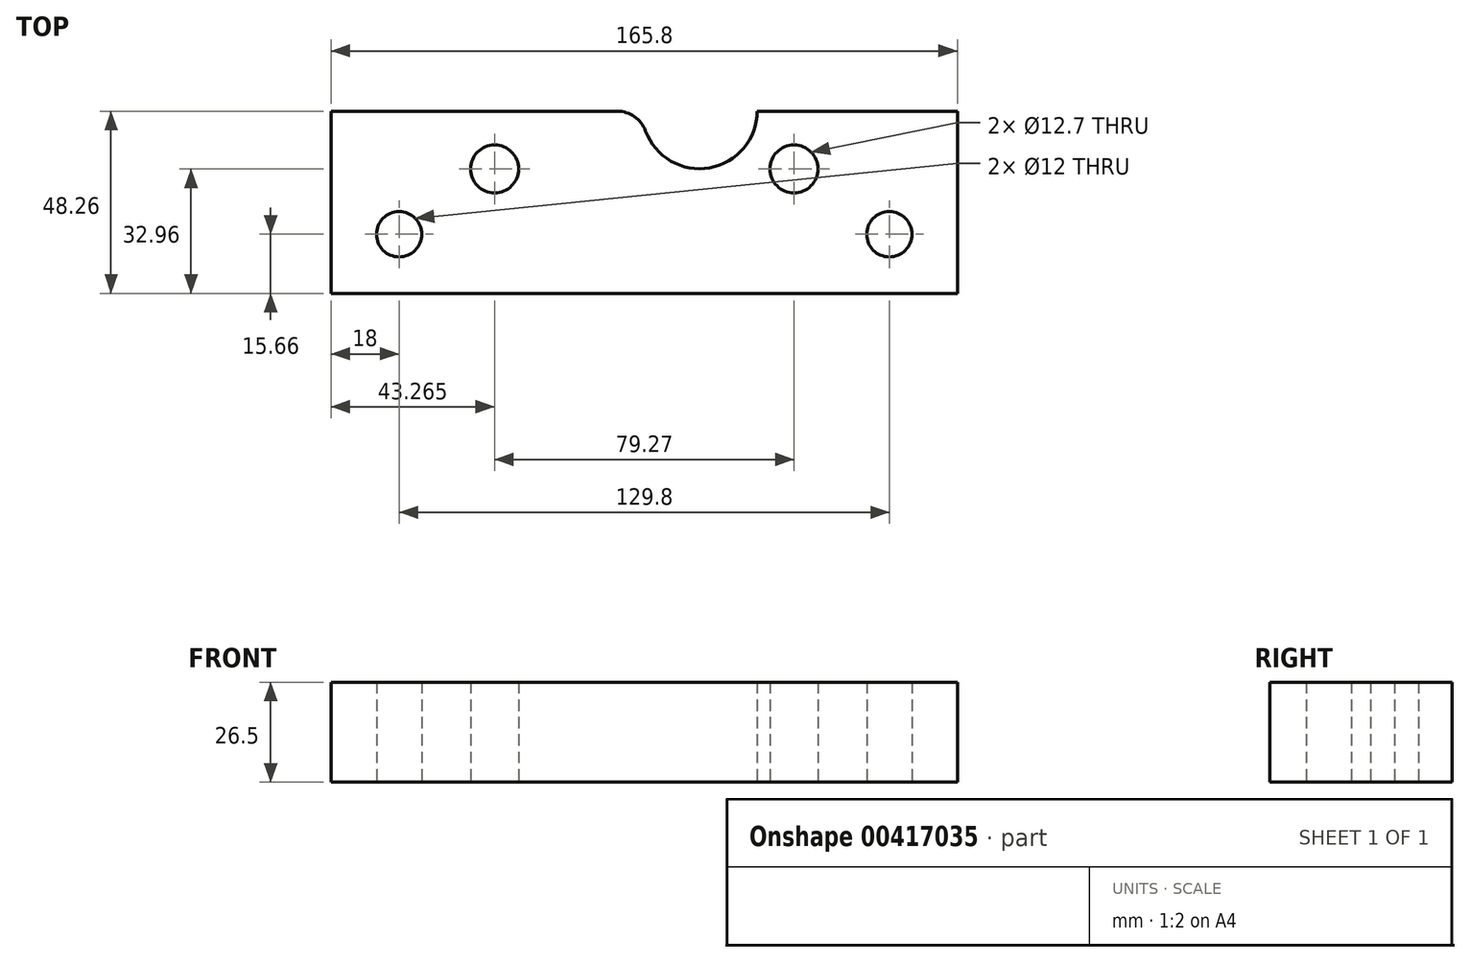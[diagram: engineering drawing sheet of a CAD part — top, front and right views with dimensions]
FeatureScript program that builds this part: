
annotation { "Feature Type Name" : "Feature", "Feature Type Description" : "" }
export const myFeature = defineFeature(function(context is Context, id is Id, definition is map)
    precondition{}
    {
        {
            var Q0;
            Q0=qCreatedBy(makeId("Top.planeOp"),FACE);
            var sketch = newSketch(context, id + "F0", { "sketchPlane" : qUnion([Q0])});
            skLineSegment(sketch, "E0.bottom", {"start": v(-82.9, 32.6) * mm, "end": v(-7.18, 32.6) * mm});
            skLineSegment(sketch, "E0.top", {"start": v(-82.9, -15.66) * mm, "end": v(82.9, -15.66) * mm});
            skLineSegment(sketch, "E0.left", {"start": v(-82.9, 32.6) * mm, "end": v(-82.9, -15.66) * mm});
            skLineSegment(sketch, "E0.right", {"start": v(82.9, 32.6) * mm, "end": v(82.9, -15.66) * mm});
            skCircle(sketch, "E1", {"center": v(-39.63, 17.3) * mm, "radius": 6.35 * mm});
            skCircle(sketch, "E2", {"center": v(39.63, 17.3) * mm, "radius": 6.35 * mm});
            skCircle(sketch, "E3", {"center": v(64.9, 0) * mm, "radius": 6 * mm});
            skCircle(sketch, "E4", {"center": v(-64.9, 0) * mm, "radius": 6 * mm});
            skPoint(sketch, "E5", {"position": v(-70.9, 0) * mm});
            skPoint(sketch, "E6", {"position": v(70.9, 0) * mm});
            skPoint(sketch, "E7", {"position": v(-58.9, 0) * mm});
            skPoint(sketch, "E8", {"position": v(58.9, 0) * mm});
            skPoint(sketch, "E9", {"position": v(-45.98, 17.3) * mm});
            skPoint(sketch, "E10", {"position": v(45.98, 17.3) * mm});
            skPoint(sketch, "E11", {"position": v(-33.28, 17.3) * mm});
            skPoint(sketch, "E12", {"position": v(33.28, 17.3) * mm});
            skArc(sketch, "E13", {"start": v(0.33, 27.35) * mm, "mid": v(17.3, 17.6) * mm, "end": v(29.87, 32.6) * mm});
            skLineSegment(sketch, "E14", {"start": v(-39.63, 17.3) * mm, "end": v(39.63, 17.3) * mm, "construction": true});
            skLineSegment(sketch, "E15", {"start": v(64.9, 0) * mm, "end": v(-64.9, 0) * mm, "construction": true});
            skLineSegment(sketch, "E16", {"start": v(0, 0) * mm, "end": v(0, 17.3) * mm, "construction": true});
            skLineSegment(sketch, "E17", {"start": v(-0.6, 32.6) * mm, "end": v(29.87, 32.6) * mm, "construction": true});
            skLineSegment(sketch, "E18", {"start": v(29.87, 32.6) * mm, "end": v(82.9, 32.6) * mm});
            skPoint(sketch, "E19.visualSharp", {"position": v(-0.6, 32.6) * mm});
            skArc(sketch, "E19.filletArc", {"start": v(0.33, 27.35) * mm, "mid": v(-2.6, 31.16) * mm, "end": v(-7.18, 32.6) * mm});
            skSolve(sketch);
        }
        {
            var Q0;
            Q0=makeQuery(id+"F0.imprint","IMPRINT",FACE,{"disambiguationData":[TD([[makeQuery(id+"F0.imprint","IMPRINT",EDGE,{"derivedFrom":sQuery(id+"F0.wireOp",EDGE,"E0.top")}),1.0]])]});
            extrude(context, id + "F1", {"entities" : qUnion([Q0]), "depth" : 26.5 * mm});
        }
    });
